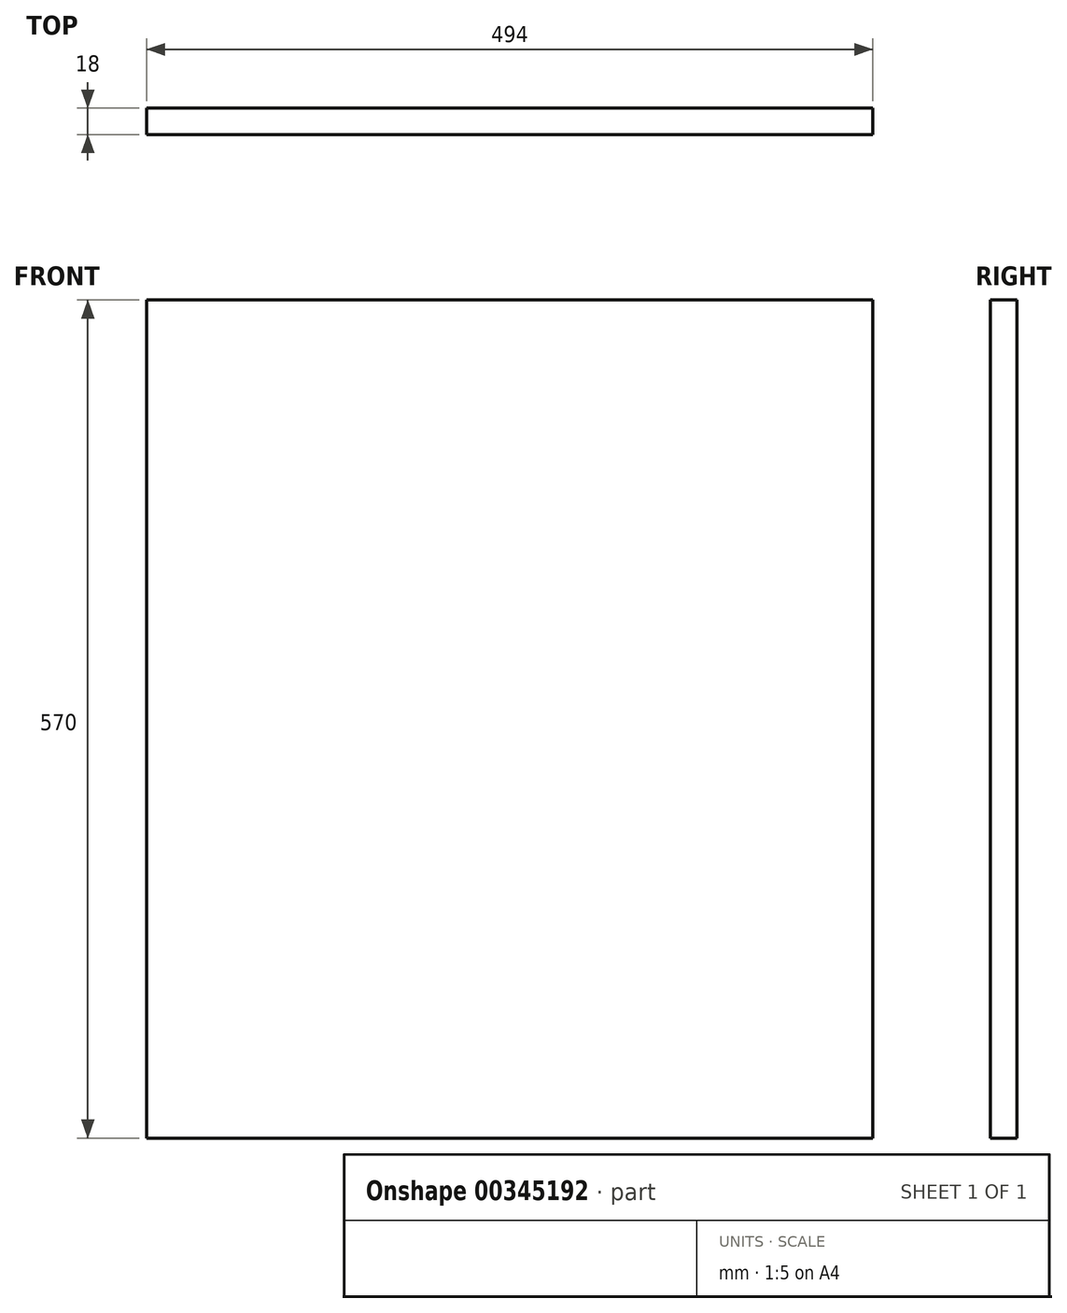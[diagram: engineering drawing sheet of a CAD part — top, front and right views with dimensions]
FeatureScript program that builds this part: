
annotation { "Feature Type Name" : "Feature", "Feature Type Description" : "" }
export const myFeature = defineFeature(function(context is Context, id is Id, definition is map)
    precondition{}
    {
        {
            var Q0;
            Q0=qCreatedBy(makeId("Front.planeOp"),FACE);
            var sketch = newSketch(context, id + "F0", { "sketchPlane" : qUnion([Q0])});
            skLineSegment(sketch, "E0.bottom", {"start": v(0, 0) * mm, "end": v(494, 0) * mm});
            skLineSegment(sketch, "E0.top", {"start": v(0, 570) * mm, "end": v(494, 570) * mm});
            skLineSegment(sketch, "E0.left", {"start": v(0, 0) * mm, "end": v(0, 570) * mm});
            skLineSegment(sketch, "E0.right", {"start": v(494, 0) * mm, "end": v(494, 570) * mm});
            skSolve(sketch);
        }
        {
            var Q0;
            Q0=makeQuery(id+"F0.imprint","IMPRINT",FACE,{"disambiguationData":[TD([[makeQuery(id+"F0.imprint","IMPRINT",EDGE,{"derivedFrom":sQuery(id+"F0.wireOp",EDGE,"E0.bottom")}),1.0]])]});
            extrude(context, id + "F1", {"entities" : qUnion([Q0]), "depth" : 18 * mm});
        }
    });
